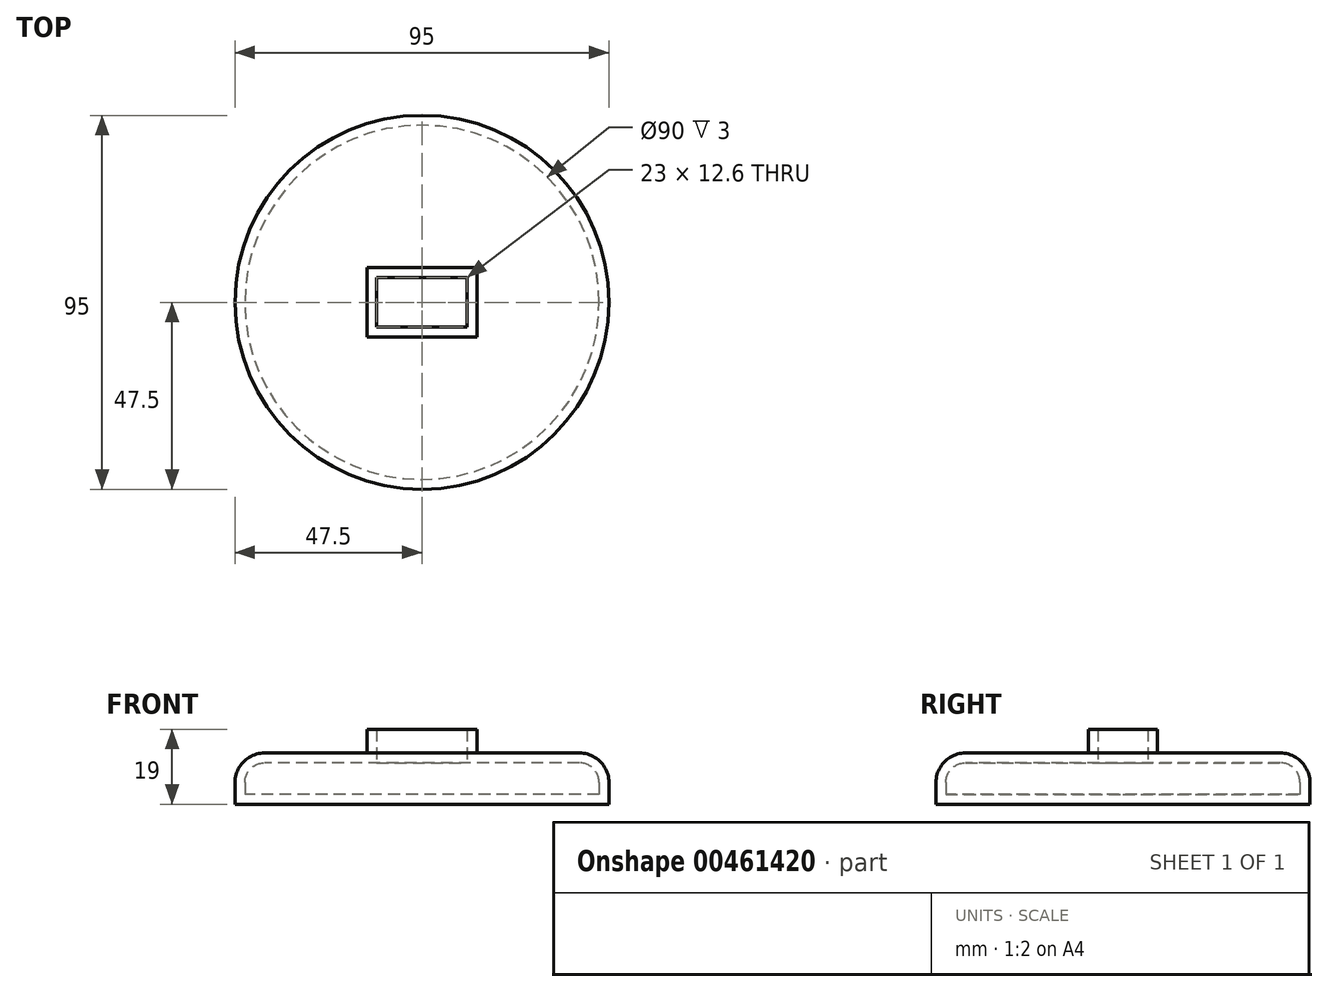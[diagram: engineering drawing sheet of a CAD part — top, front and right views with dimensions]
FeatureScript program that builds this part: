
annotation { "Feature Type Name" : "Feature", "Feature Type Description" : "" }
export const myFeature = defineFeature(function(context is Context, id is Id, definition is map)
    precondition{}
    {
        {
            var Q0;
            Q0=qCreatedBy(makeId("Top.planeOp"),FACE);
            var sketch = newSketch(context, id + "F0", { "sketchPlane" : qUnion([Q0])});
            skCircle(sketch, "E0", {"center": v(0, 0) * mm, "radius": 45 * mm});
            skSolve(sketch);
        }
        {
            var Q0;
            Q0 = qSketchRegion(id + "F0", true);
            extrude(context, id + "F1", {"entities" : qUnion([Q0]), "depth" : 8 * mm});
        }
        {
            var Q0;
            Q0=makeQuery(id+"F1.opExtrude","CAP_EDGE",EDGE,{"disambiguationData":[OSD([sQuery(id+"F0.wireOp",EDGE,"E0")])],"isStart":false});
            fillet(context, id + "F2", {"entities" : qUnion([Q0]), "radius" : 5 * mm, "tangentPropagation" : true, "allowEdgeOverflow" : false});
        }
        {
            var Q0;
            Q0=qCreatedBy(makeId("Top.planeOp"),FACE);
            var sketch = newSketch(context, id + "F3", { "sketchPlane" : qUnion([Q0])});
            skLineSegment(sketch, "E1.bottom", {"start": v(11.5, 6.3) * mm, "end": v(-11.5, 6.3) * mm});
            skLineSegment(sketch, "E1.top", {"start": v(11.5, -6.3) * mm, "end": v(-11.5, -6.3) * mm});
            skLineSegment(sketch, "E1.left", {"start": v(11.5, 6.3) * mm, "end": v(11.5, -6.3) * mm});
            skLineSegment(sketch, "E1.right", {"start": v(-11.5, 6.3) * mm, "end": v(-11.5, -6.3) * mm});
            skPoint(sketch, "E1.middle", {"position": v(0, 0) * mm});
            skSolve(sketch);
        }
        {
            var Q0;
            Q0 = qSketchRegion(id + "F3", true);
            extrude(context, id + "F4", {"entities" : qUnion([Q0]), "operationType" : NewBodyOperationType.ADD, "depth" : 16.5 * mm});
        }
        {
            var Q0;
            Q0=makeQuery(id+"F4.opExtrude","CAP_FACE",FACE,{"disambiguationData":[OSD([sQuery(id+"F3.wireOp",EDGE,"E1.bottom"),sQuery(id+"F3.wireOp",EDGE,"E1.top"),sQuery(id+"F3.wireOp",EDGE,"E1.left"),sQuery(id+"F3.wireOp",EDGE,"E1.right")])],"isStart":false});
            shell(context, id + "F5", {"entities" : qUnion([Q0]), "thickness" : 2.5 * mm, "oppositeDirection" : true});
        }
    });
